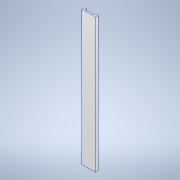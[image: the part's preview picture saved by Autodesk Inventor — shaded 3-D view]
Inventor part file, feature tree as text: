
AUTODESK INVENTOR PART (.ipt)
format: ipt  version: 2022 (Build 260153000, 153)  size: 103,424 bytes
history: native  units: mm
features: extrude x1, sketch x1
ambient origin geometry x8: Origin, YZ Plane, XZ Plane, XY Plane, X Axis, Y Axis, Z Axis, Center Point
bodies: Solid1 (feature_tree)
feature tree (2):
  extrude  "Extrusion1"  Depth=100.0mm
  sketch  "Sketch1"  dims[d0=20.0mm d1=100.0mm d2=1000.0mm d3=0.0mm d4=10.0mm d5=16.0mm d6=16.0mm]
